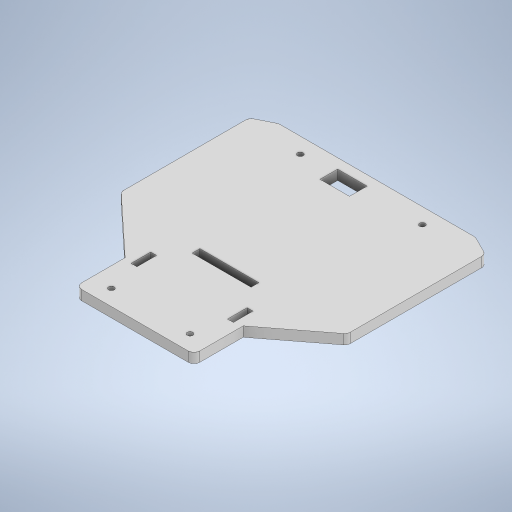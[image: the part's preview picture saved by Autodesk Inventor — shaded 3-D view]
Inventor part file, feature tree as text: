
AUTODESK INVENTOR PART (.ipt)
format: ipt  version: 2023 (Build 270158000, 158)  size: 313,344 bytes
history: native  units: in
note: dims shown in document units (in); Inventor stores cm internally (conversion verified against a paired STEP export)
features: extrude x2, sketch x2, fillet x1
ambient origin geometry x8: Origin, YZ Plane, XZ Plane, XY Plane, X Axis, Y Axis, Z Axis, Center Point
bodies: Solid1 (feature_tree)
feature tree (5):
  extrude  "Extrusion1"  Depth=2.7559in
  fillet  "Fillet1"  Radius=2.7559in
  extrude  "Extrusion2"  Depth=0.7874in
  sketch  "Sketch1"  dims[d0=4.7244in d1=5.9055in d18=2.7559in d43=2.1654in d44=2.7559in]
  sketch  "Sketch2"  dims[d45=1.378in d46=0.7874in d47=1.5748in d48=0.1102in d49=0.1102in d50=0.9843in d51=0.9843in d52=0.1575in d53=0.315in d54=0.1575in d55=0.315in d56=0.1102in d57=0.1102in d58=0.1969in d59=0.0in d60=0.1181in d61=0.3937in d62=1.1811in d63=0.2362in d64=0.1969in d65=90.0deg d68=0.5906in d69=0.3543in d70=0.0in d71=0.0in d73=0.9843in d74=0.9843in d76=2.5591in d77=0.9055in d78=1.811in d79=0.1181in d80=0.7874in d81=0.1181in d82=0.7874in d83=0.3937in d84=0.3937in d85=1.1811in d86=0.1575in d87=0.1102in]
